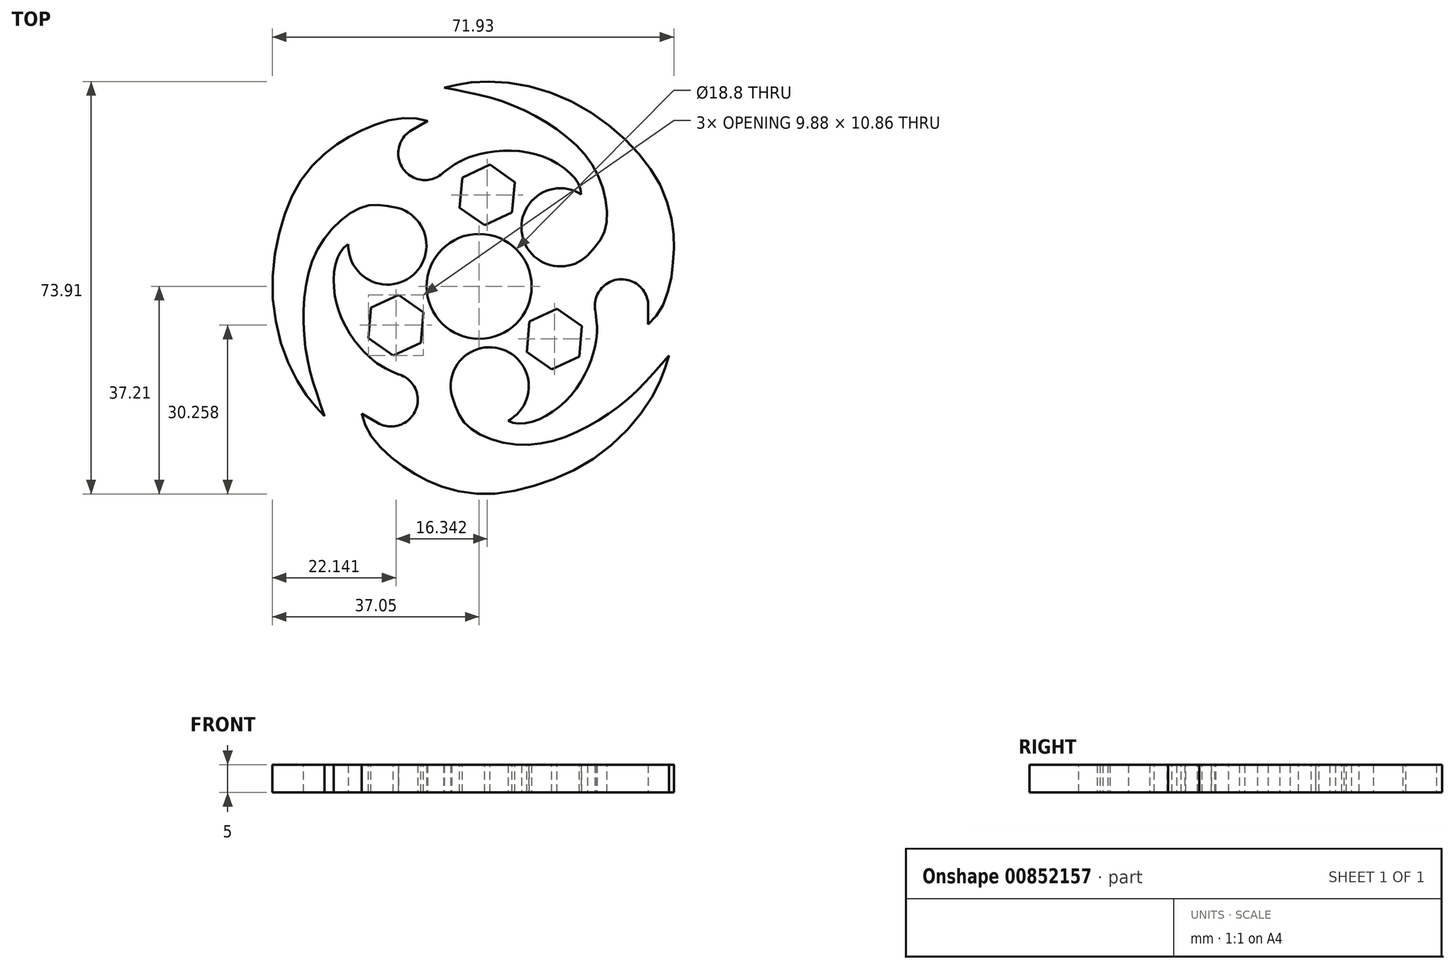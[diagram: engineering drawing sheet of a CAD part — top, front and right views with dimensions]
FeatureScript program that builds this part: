
annotation { "Feature Type Name" : "Feature", "Feature Type Description" : "" }
export const myFeature = defineFeature(function(context is Context, id is Id, definition is map)
    precondition{}
    {
        {
            var Q0;
            Q0=qCreatedBy(makeId("Top.planeOp"),FACE);
            var sketch = newSketch(context, id + "F0", { "sketchPlane" : qUnion([Q0])});
            skCircle(sketch, "E0", {"center": v(0, 0) * mm, "radius": 9.4 * mm, "construction": true});
            skCircle(sketch, "E1", {"center": v(0, 0) * mm, "radius": 11 * mm, "construction": true});
            skPoint(sketch, "E2.orphan", {"position": v(-0.16, 0.1) * mm});
            skLineSegment(sketch, "E3", {"start": v(0, 0) * mm, "end": v(54.2, 0) * mm, "construction": true});
            skLineSegment(sketch, "E4", {"start": v(0, 0) * mm, "end": v(46.96, 34.12) * mm, "construction": true});
            skPoint(sketch, "E5", {"position": v(18.27, 16.52) * mm});
            skPoint(sketch, "E6", {"position": v(19.37, 5.5) * mm});
            skFitSpline(sketch, "E7", {"points": [v(18.27, 16.52) * mm, v(14.9, 21.44) * mm, v(5.63, 24.33) * mm, v(-2.05, 23.03) * mm, v(-6.38, 20.42) * mm], "startDerivative": vector(1.06, 21.36) * mm, "endDerivative": vector(-29.74, -21.68) * mm});
            skPoint(sketch, "E8", {"position": v(-12.46, 27.57) * mm});
            skLineSegment(sketch, "E9", {"start": v(-12.46, 27.57) * mm, "end": v(-9.25, 29.62) * mm});
            skArc(sketch, "E10", {"start": v(-12.46, 27.57) * mm, "mid": v(-13.51, 20.5) * mm, "end": v(-6.38, 20.42) * mm, "construction": true});
            skLineSegment(sketch, "E11", {"start": v(-9.25, 29.62) * mm, "end": v(0, 0) * mm, "construction": true});
            skLineSegment(sketch, "E12", {"start": v(0, 0) * mm, "end": v(20.87, -4.69) * mm, "construction": true});
            skFitSpline(sketch, "E13", {"points": [v(19.37, 5.5) * mm, v(22.8, 11.23) * mm, v(20.76, 20.87) * mm, v(13.06, 28.72) * mm, v(3.47, 33.38) * mm, v(-6.26, 35.63) * mm], "startDerivative": vector(34.03, 36.44) * mm, "endDerivative": vector(-46.4, 9.15) * mm});
            skArc(sketch, "E14", {"start": v(18.27, 16.52) * mm, "mid": v(7.6, 9.88) * mm, "end": v(19.37, 5.5) * mm});
            skFitSpline(sketch, "E15", {"points": [v(-6.26, 35.63) * mm, v(-1.76, 36.51) * mm, v(6.78, 36.27) * mm, v(18.35, 32.18) * mm, v(27.26, 25.2) * mm, v(32.47, 18.1) * mm, v(34.65, 10.9) * mm, v(34.83, 5.8) * mm, v(34.23, 0.68) * mm, v(32.5, -4.12) * mm, v(30.28, -6.8) * mm], "startDerivative": vector(50.97, 12.47) * mm, "endDerivative": vector(-33.27, -33.38) * mm});
            skPoint(sketch, "E16", {"position": v(-5.18, 7.84) * mm});
            skPoint(sketch, "E17", {"position": v(9.17, -2.06) * mm});
            skArc(sketch, "E18", {"start": v(-5.18, 7.84) * mm, "mid": v(5.34, 7.74) * mm, "end": v(9.17, -2.06) * mm});
            skLineSegment(sketch, "E19", {"start": v(9.17, -2.06) * mm, "end": v(20.87, -4.69) * mm});
            skPoint(sketch, "E20", {"position": v(20.87, -4.69) * mm});
            skLineSegment(sketch, "E21", {"start": v(30.28, -6.8) * mm, "end": v(30.28, -3.5) * mm});
            skArc(sketch, "E22", {"start": v(30.28, -3.5) * mm, "mid": v(24.9, 1.24) * mm, "end": v(20.87, -4.69) * mm});
            skLineSegment(sketch, "E23", {"start": v(-6.38, 20.42) * mm, "end": v(0, 0) * mm});
            skSolve(sketch);
        }
        {
            var Q0;
            {var subQ1=sQuery(id+"F0.wireOp",EDGE,"E7");Q0=makeQuery(id+"F0.imprint","IMPRINT",FACE,{"disambiguationData":[TD([[makeQuery(id+"F0.imprint","IMPRINT",EDGE,{"derivedFrom":subQ1}),1.0]])]});}
            var Q1;
            {var subQ3=sQuery(id+"F0.wireOp",EDGE,"vHKPbalO-4eth-BBEX-WpL6-SEu3oY2ButND");Q1=makeQuery(id+"F0.imprint","IMPRINT",FACE,{"disambiguationData":[TD([[makeQuery(id+"F0.imprint","IMPRINT",EDGE,{"derivedFrom":subQ3}),-1.0]])]});}
            extrude(context, id + "F1", {"entities" : qUnion([Q0, Q1]), "depth" : 5 * mm, "offsetDistance" : 25 * mm});
        }
        {
            var Q0;
            Q0=qCreatedBy(makeId("Front.planeOp"),FACE);
            var sketch = newSketch(context, id + "F2", { "sketchPlane" : qUnion([Q0])});
            skLineSegment(sketch, "E24", {"start": v(0, 0) * mm, "end": v(0, 55.86) * mm, "construction": true});
            skSolve(sketch);
        }
        {
            var Q0;
            Q0=makeQuery(id+"F1.opExtrude","SWEPT_BODY",BODY,{"disambiguationData":[OSD([sQuery(id+"F0.wireOp",EDGE,"E10"),sQuery(id+"F0.wireOp",EDGE,"zojvIL6C-BE0k-co1T-s1hC-A86PAPgQTmRn"),sQuery(id+"F0.wireOp",EDGE,"vHKPbalO-4eth-BBEX-WpL6-SEu3oY2ButND")])]});
            var Q1;
            Q1=makeQuery(id+"F1.opExtrude","SWEPT_BODY",BODY,{"disambiguationData":[OSD([sQuery(id+"F0.wireOp",EDGE,"E7"),sQuery(id+"F0.wireOp",EDGE,"E10"),sQuery(id+"F0.wireOp",EDGE,"E13"),sQuery(id+"F0.wireOp",EDGE,"E14"),sQuery(id+"F0.wireOp",EDGE,"E15"),sQuery(id+"F0.wireOp",EDGE,"E18"),sQuery(id+"F0.wireOp",EDGE,"7hLGK6TZ-VlNH-Qm4p-4Afw-j84KGP8fiYRH"),sQuery(id+"F0.wireOp",EDGE,"E19")])]});
            var Q2;
            Q2=sQuery(id+"F2.wireOp",EDGE,"E24");
            circularPattern(context, id + "F3", {"operationType" : NewBodyOperationType.ADD, "entities" : qUnion([Q0, Q1]), "axis" : qUnion([Q2]), "angle" : 360 * degree, "instanceCount" : 3, "equalSpace" : true});
        }
        {
            var Q0;
            {var subQ0=makeQuery(id+"F1.opExtrude","CAP_FACE",FACE,{"disambiguationData":[OSD([sQuery(id+"F0.wireOp",EDGE,"E7"),sQuery(id+"F0.wireOp",EDGE,"E13"),sQuery(id+"F0.wireOp",EDGE,"E14"),sQuery(id+"F0.wireOp",EDGE,"E15"),sQuery(id+"F0.wireOp",EDGE,"E18"),sQuery(id+"F0.wireOp",EDGE,"E19"),sQuery(id+"F0.wireOp",EDGE,"E21"),sQuery(id+"F0.wireOp",EDGE,"E22"),sQuery(id+"F0.wireOp",EDGE,"E23")])],"isStart":false});Q0=makeQuery(id+"F3.boolean.opBoolean","MERGE",FACE,{"derivedFrom":[subQ0,makeQuery(id+"F3.opPattern","COPY",FACE,{"derivedFrom":subQ0,"instanceName":"1"}),makeQuery(id+"F3.opPattern","COPY",FACE,{"derivedFrom":subQ0,"instanceName":"2"})]});}
            var sketch = newSketch(context, id + "F4", { "sketchPlane" : qUnion([Q0])});
            skLineSegment(sketch, "E25", {"start": v(0, 0) * mm, "end": v(5, 57.07) * mm, "construction": true});
            skLineSegment(sketch, "E26", {"start": v(0, 0) * mm, "end": v(72.72, -50.92) * mm, "construction": true});
            skCircle(sketch, "E27.cCircle", {"center": v(1.43, 16.39) * mm, "radius": 5.45 * mm, "construction": true});
            skLineSegment(sketch, "E27.0", {"start": v(0.96, 10.96) * mm, "end": v(-3.5, 14.08) * mm});
            skLineSegment(sketch, "E27.1", {"start": v(-3.5, 14.08) * mm, "end": v(-3.03, 19.51) * mm});
            skLineSegment(sketch, "E27.2", {"start": v(-3.03, 19.51) * mm, "end": v(1.9, 21.82) * mm});
            skLineSegment(sketch, "E27.3", {"start": v(1.9, 21.82) * mm, "end": v(6.37, 18.7) * mm});
            skLineSegment(sketch, "E27.4", {"start": v(6.37, 18.7) * mm, "end": v(5.9, 13.26) * mm});
            skLineSegment(sketch, "E27.5", {"start": v(5.9, 13.26) * mm, "end": v(0.96, 10.96) * mm});
            skLineSegment(sketch, "E28.1.0", {"start": v(-19.85, -9.26) * mm, "end": v(-19.37, -3.83) * mm});
            skLineSegment(sketch, "E28.1.1", {"start": v(-19.37, -3.83) * mm, "end": v(-14.43, -1.52) * mm});
            skLineSegment(sketch, "E28.1.2", {"start": v(-14.43, -1.52) * mm, "end": v(-9.97, -4.65) * mm});
            skLineSegment(sketch, "E28.1.3", {"start": v(-9.97, -4.65) * mm, "end": v(-10.44, -10.08) * mm});
            skLineSegment(sketch, "E28.1.4", {"start": v(-10.44, -10.08) * mm, "end": v(-15.38, -12.38) * mm});
            skLineSegment(sketch, "E28.1.5", {"start": v(-15.38, -12.38) * mm, "end": v(-19.85, -9.26) * mm});
            skLineSegment(sketch, "E28.2.0", {"start": v(17.94, -12.56) * mm, "end": v(13, -14.86) * mm});
            skLineSegment(sketch, "E28.2.1", {"start": v(13, -14.86) * mm, "end": v(8.54, -11.74) * mm});
            skLineSegment(sketch, "E28.2.2", {"start": v(8.54, -11.74) * mm, "end": v(9.01, -6.3) * mm});
            skLineSegment(sketch, "E28.2.3", {"start": v(9.01, -6.3) * mm, "end": v(13.95, -4) * mm});
            skLineSegment(sketch, "E28.2.4", {"start": v(13.95, -4) * mm, "end": v(18.41, -7.13) * mm});
            skLineSegment(sketch, "E28.2.5", {"start": v(18.41, -7.13) * mm, "end": v(17.94, -12.56) * mm});
            skPoint(sketch, "E28.center", {"position": v(0, 0) * mm});
            skLineSegment(sketch, "E29", {"start": v(0, 0) * mm, "end": v(42.82, 11.47) * mm, "construction": true});
            skCircle(sketch, "E30.cCircle", {"center": v(28.32, 7.59) * mm, "radius": 5.45 * mm, "construction": true});
            skLineSegment(sketch, "E30.0", {"start": v(33.59, 9) * mm, "end": v(32.18, 3.73) * mm});
            skLineSegment(sketch, "E30.1", {"start": v(32.18, 3.73) * mm, "end": v(26.91, 2.32) * mm});
            skLineSegment(sketch, "E30.2", {"start": v(26.91, 2.32) * mm, "end": v(23.06, 6.18) * mm});
            skLineSegment(sketch, "E30.3", {"start": v(23.06, 6.18) * mm, "end": v(24.47, 11.44) * mm});
            skLineSegment(sketch, "E30.4", {"start": v(24.47, 11.44) * mm, "end": v(29.73, 12.85) * mm});
            skLineSegment(sketch, "E30.5", {"start": v(29.73, 12.85) * mm, "end": v(33.59, 9) * mm});
            skLineSegment(sketch, "E31.1.0", {"start": v(-24.59, 24.59) * mm, "end": v(-19.32, 26) * mm});
            skLineSegment(sketch, "E31.1.1", {"start": v(-26, 19.32) * mm, "end": v(-24.59, 24.59) * mm});
            skLineSegment(sketch, "E31.1.2", {"start": v(-22.14, 15.47) * mm, "end": v(-26, 19.32) * mm});
            skLineSegment(sketch, "E31.1.3", {"start": v(-16.88, 16.88) * mm, "end": v(-22.14, 15.47) * mm});
            skLineSegment(sketch, "E31.1.4", {"start": v(-15.47, 22.14) * mm, "end": v(-16.88, 16.88) * mm});
            skLineSegment(sketch, "E31.1.5", {"start": v(-19.32, 26) * mm, "end": v(-15.47, 22.14) * mm});
            skLineSegment(sketch, "E31.2.0", {"start": v(-9, -33.59) * mm, "end": v(-12.85, -29.73) * mm});
            skLineSegment(sketch, "E31.2.1", {"start": v(-3.73, -32.18) * mm, "end": v(-9, -33.59) * mm});
            skLineSegment(sketch, "E31.2.2", {"start": v(-2.32, -26.91) * mm, "end": v(-3.73, -32.18) * mm});
            skLineSegment(sketch, "E31.2.3", {"start": v(-6.18, -23.06) * mm, "end": v(-2.32, -26.91) * mm});
            skLineSegment(sketch, "E31.2.4", {"start": v(-11.44, -24.47) * mm, "end": v(-6.18, -23.06) * mm});
            skLineSegment(sketch, "E31.2.5", {"start": v(-12.85, -29.73) * mm, "end": v(-11.44, -24.47) * mm});
            skSolve(sketch);
        }
        {
            var Q0;
            Q0=makeQuery(id+"F4.imprint","IMPRINT",FACE,{"disambiguationData":[TD([[makeQuery(id+"F4.imprint","IMPRINT",EDGE,{"derivedFrom":sQuery(id+"F4.wireOp",EDGE,"E27.0")}),-1.0]])]});
            var Q1;
            Q1=makeQuery(id+"F4.imprint","IMPRINT",FACE,{"disambiguationData":[TD([[makeQuery(id+"F4.imprint","IMPRINT",EDGE,{"derivedFrom":sQuery(id+"F4.wireOp",EDGE,"E28.2.0")}),-1.0]])]});
            var Q2;
            Q2=makeQuery(id+"F4.imprint","IMPRINT",FACE,{"disambiguationData":[TD([[makeQuery(id+"F4.imprint","IMPRINT",EDGE,{"derivedFrom":sQuery(id+"F4.wireOp",EDGE,"E28.1.0")}),-1.0]])]});
            extrude(context, id + "F5", {"entities" : qUnion([Q0, Q1, Q2]), "operationType" : NewBodyOperationType.REMOVE, "oppositeDirection" : true, "depth" : 25 * mm, "offsetDistance" : 25 * mm});
        }
    });
